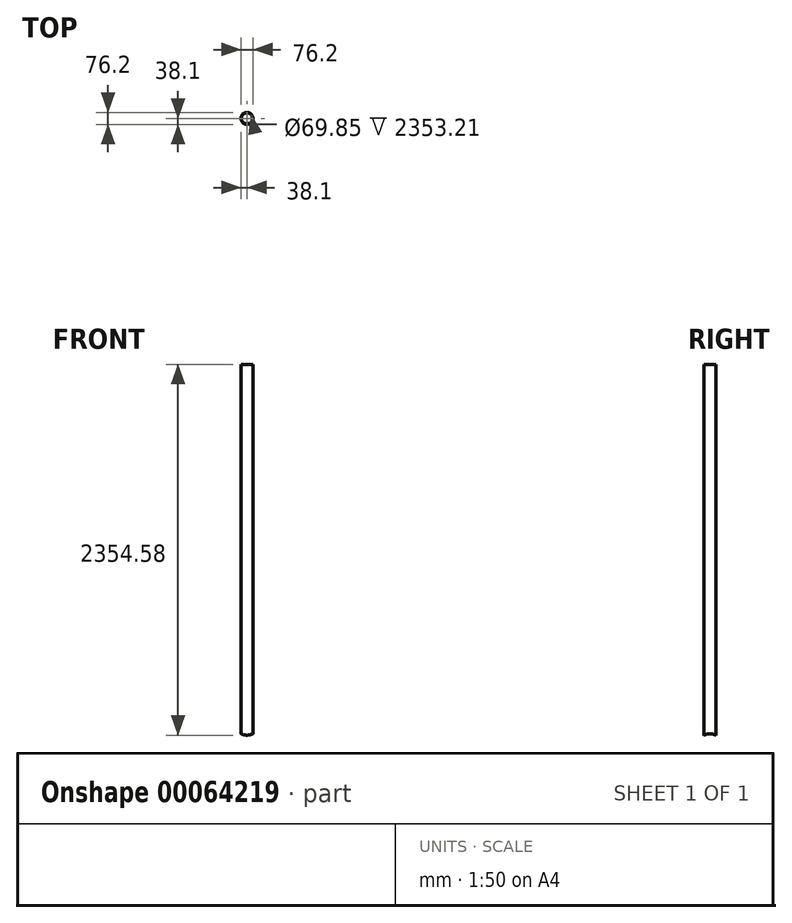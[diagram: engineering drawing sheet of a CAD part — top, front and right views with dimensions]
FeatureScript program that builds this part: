
annotation { "Feature Type Name" : "Feature", "Feature Type Description" : "" }
export const myFeature = defineFeature(function(context is Context, id is Id, definition is map)
    precondition{}
    {
        {
            var Q0;
            Q0=qCreatedBy(makeId("Top.planeOp"),FACE);
            var sketch = newSketch(context, id + "F0", { "sketchPlane" : qUnion([Q0])});
            skCircle(sketch, "E0", {"center": v(0, 0) * mm, "radius": 38.1 * mm});
            skSolve(sketch);
        }
        {
            var Q0;
            Q0 = qSketchRegion(id + "F0", true);
            extrude(context, id + "F1", {"entities" : qUnion([Q0]), "depth" : 2438.4 * mm});
        }
        {
            var Q0;
            Q0=qCreatedBy(makeId("Top.planeOp"),FACE);
            var sketch = newSketch(context, id + "F2", { "sketchPlane" : qUnion([Q0])});
            skCircle(sketch, "E1", {"center": v(0, 0) * mm, "radius": 34.93 * mm});
            skSolve(sketch);
        }
        {
            var Q0;
            Q0 = qSketchRegion(id + "F2", true);
            extrude(context, id + "F3", {"entities" : qUnion([Q0]), "operationType" : NewBodyOperationType.REMOVE, "endBound" : BoundingType.THROUGH_ALL, "depth" : 25.4 * mm});
        }
        {
            var Q0;
            Q0=qCreatedBy(makeId("Right.planeOp"),FACE);
            var sketch = newSketch(context, id + "F4", { "sketchPlane" : qUnion([Q0])});
            skCircle(sketch, "E2", {"center": v(0, 0) * mm, "radius": 92.08 * mm});
            skSolve(sketch);
        }
        {
            var Q0;
            Q0=makeQuery(id+"F4.imprint","IMPRINT",FACE,{"disambiguationData":[TD([[makeQuery(id+"F4.imprint","IMPRINT",EDGE,{"derivedFrom":sQuery(id+"F4.wireOp",EDGE,"E2")}),1.0]])]});
            extrude(context, id + "F5", {"entities" : qUnion([Q0]), "operationType" : NewBodyOperationType.REMOVE, "endBound" : BoundingType.SYMMETRIC, "oppositeDirection" : true, "depth" : 152.4 * mm});
        }
    });
